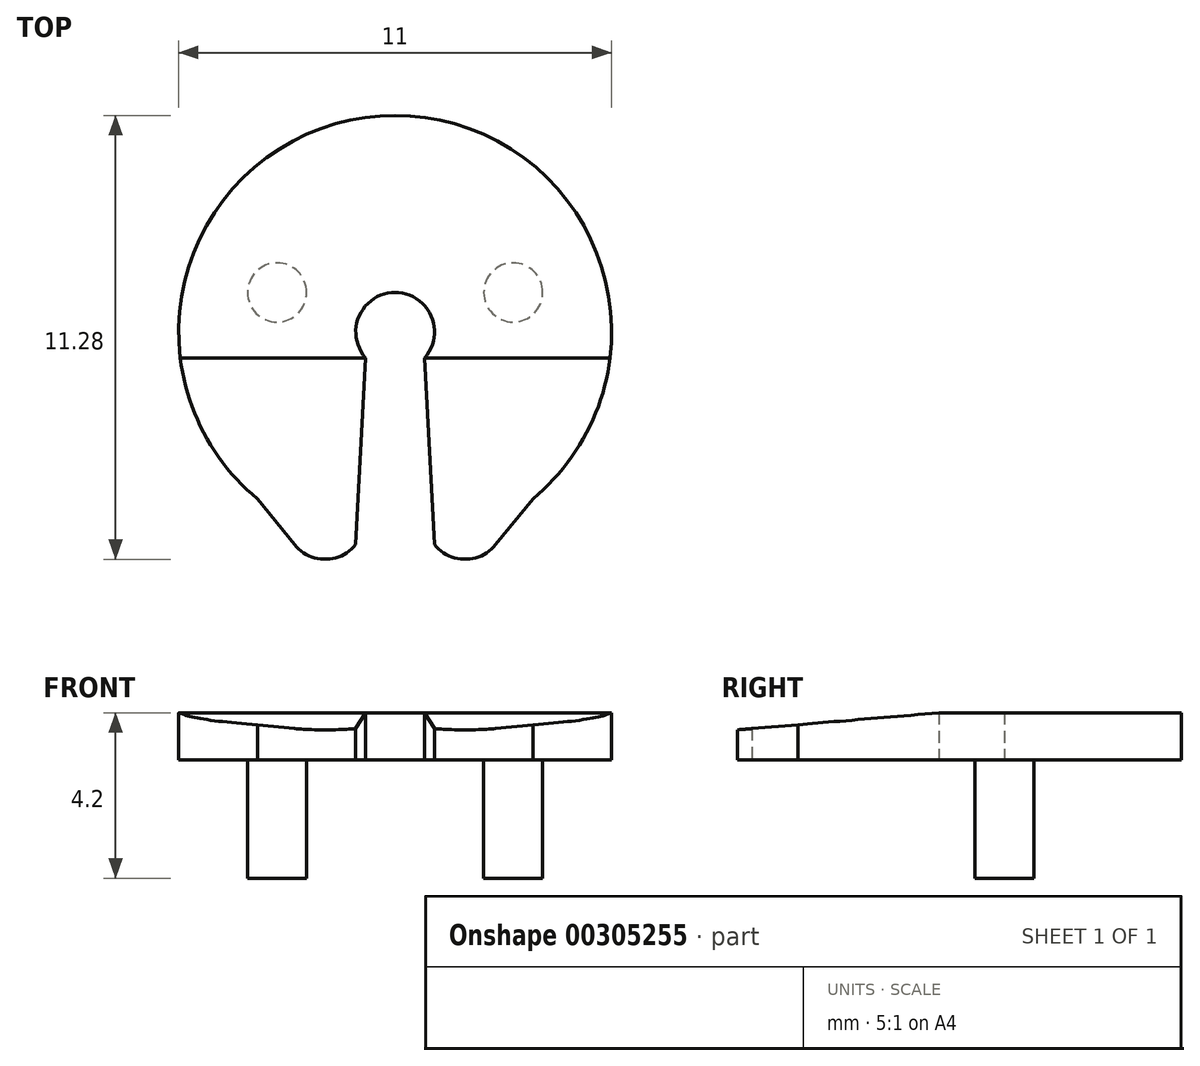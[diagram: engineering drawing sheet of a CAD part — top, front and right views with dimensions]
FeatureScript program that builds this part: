
annotation { "Feature Type Name" : "Feature", "Feature Type Description" : "" }
export const myFeature = defineFeature(function(context is Context, id is Id, definition is map)
    precondition{}
    {
        {
            var Q0;
            Q0=qCreatedBy(makeId("Top.planeOp"),FACE);
            var sketch = newSketch(context, id + "F0", { "sketchPlane" : qUnion([Q0])});
            skArc(sketch, "E0", {"start": v(0.75, -0.66) * mm, "mid": v(0, 1) * mm, "end": v(-0.75, -0.66) * mm});
            skArc(sketch, "E1", {"start": v(3.5, -4.24) * mm, "mid": v(0, 5.5) * mm, "end": v(-3.5, -4.24) * mm});
            skLineSegment(sketch, "E2", {"start": v(-3.5, -4.24) * mm, "end": v(3.5, -4.24) * mm, "construction": true});
            skLineSegment(sketch, "E3", {"start": v(-1, -5.4) * mm, "end": v(1, -5.4) * mm, "construction": true});
            skLineSegment(sketch, "E4", {"start": v(-0.75, -0.66) * mm, "end": v(-1, -5.4) * mm});
            skLineSegment(sketch, "E5", {"start": v(0.75, -0.66) * mm, "end": v(1, -5.4) * mm});
            skLineSegment(sketch, "E6", {"start": v(-0.75, -0.66) * mm, "end": v(0.75, -0.66) * mm, "construction": true});
            skLineSegment(sketch, "E7", {"start": v(3.5, -4.24) * mm, "end": v(2.56, -5.4) * mm});
            skLineSegment(sketch, "E8", {"start": v(-3.5, -4.24) * mm, "end": v(-2.56, -5.4) * mm});
            skArc(sketch, "E9", {"start": v(-2.56, -5.4) * mm, "mid": v(-1.78, -5.78) * mm, "end": v(-1, -5.4) * mm});
            skArc(sketch, "E10.MirrorCS", {"start": v(2.56, -5.4) * mm, "mid": v(1.78, -5.78) * mm, "end": v(1, -5.4) * mm});
            skLineSegment(sketch, "E11", {"start": v(0, 1) * mm, "end": v(3, 1) * mm, "construction": true});
            skCircle(sketch, "E12", {"center": v(3, 1) * mm, "radius": 0.75 * mm, "construction": true});
            skLineSegment(sketch, "E13.MirrorCS", {"start": v(0, 1) * mm, "end": v(-3, 1) * mm, "construction": true});
            skCircle(sketch, "E14.MirrorC", {"center": v(-3, 1) * mm, "radius": 0.75 * mm, "construction": true});
            skSolve(sketch);
        }
        {
            var Q0;
            Q0=makeQuery(id+"F0.imprint","IMPRINT",FACE,{"disambiguationData":[TD([[makeQuery(id+"F0.imprint","IMPRINT",EDGE,{"derivedFrom":sQuery(id+"F0.wireOp",EDGE,"E0")}),-1.0]])]});
            extrude(context, id + "F1", {"entities" : qUnion([Q0]), "depth" : 1.2 * mm});
        }
        {
            var Q0;
            Q0=qCreatedBy(makeId("Top.planeOp"),FACE);
            var sketch = newSketch(context, id + "F2", { "sketchPlane" : qUnion([Q0])});
            skCircle(sketch, "E15.0", {"center": v(-3, 1) * mm, "radius": 0.75 * mm});
            skCircle(sketch, "E16.0", {"center": v(3, 1) * mm, "radius": 0.75 * mm});
            skSolve(sketch);
        }
        {
            var Q0;
            Q0 = qSketchRegion(id + "F2", true);
            extrude(context, id + "F3", {"entities" : qUnion([Q0]), "operationType" : NewBodyOperationType.ADD, "oppositeDirection" : true, "depth" : 3 * mm});
        }
        {
            var Q0;
            Q0=makeQuery(id+"F1.opExtrude","SWEPT_FACE",FACE,{"disambiguationData":[OSD([sQuery(id+"F0.wireOp",EDGE,"E4")])]});
            var sketch = newSketch(context, id + "F4", { "sketchPlane" : qUnion([Q0])});
            skLineSegment(sketch, "E17", {"start": v(-5.45, 0) * mm, "end": v(-5.45, 0.8) * mm, "construction": true});
            skSolve(sketch);
        }
        {
            var Q0;
            Q0=makeQuery(id+"F1.opExtrude","CAP_VERTEX",VERTEX,{"disambiguationData":[OSD([sQuery(id+"F0.wireOp",EDGE,"E0"),sQuery(id+"F0.wireOp",EDGE,"E4")])],"isStart":false});
            var Q1;
            Q1=makeQuery(id+"F1.opExtrude","CAP_VERTEX",VERTEX,{"disambiguationData":[OSD([sQuery(id+"F0.wireOp",EDGE,"E0"),sQuery(id+"F0.wireOp",EDGE,"E5")])],"isStart":false});
            var Q2;
            Q2=sQuery(id+"F4.wireOp",VERTEX,"E17.end");
            cPlane(context, id + "F5", {"entities" : qUnion([Q0, Q1, Q2]), "cplaneType" : CPlaneType.THREE_POINT, "offset" : 25 * mm, "width" : 150 * mm, "height" : 150 * mm});
        }
        {
            var Q0;
            Q0=qCreatedBy(id+"F5.planeOp",FACE);
            var sketch = newSketch(context, id + "F6", { "sketchPlane" : qUnion([Q0])});
            skLineSegment(sketch, "E18", {"start": v(-0.75, -0.56) * mm, "end": v(-5.46, -0.56) * mm});
            skLineSegment(sketch, "E19", {"start": v(5.46, -0.56) * mm, "end": v(0.75, -0.56) * mm});
            skLineSegment(sketch, "E20.bottom", {"start": v(-5.46, -0.56) * mm, "end": v(5.46, -0.56) * mm});
            skLineSegment(sketch, "E20.top", {"start": v(-5.46, -5.93) * mm, "end": v(5.46, -5.93) * mm});
            skLineSegment(sketch, "E20.left", {"start": v(-5.46, -0.56) * mm, "end": v(-5.46, -5.93) * mm});
            skLineSegment(sketch, "E20.right", {"start": v(5.46, -0.56) * mm, "end": v(5.46, -5.93) * mm});
            skPoint(sketch, "E21.0.start.orphan", {"position": v(-3.5, -4.13) * mm});
            skPoint(sketch, "E22.0.start.orphan", {"position": v(-2.56, -5.29) * mm});
            skPoint(sketch, "E23.0.end.orphan", {"position": v(-1, -5.29) * mm});
            skPoint(sketch, "E23.0.start.orphan", {"position": v(-0.75, -0.56) * mm});
            skPoint(sketch, "E24.0.start.orphan", {"position": v(0.75, -0.56) * mm});
            skPoint(sketch, "E25.0.start.orphan", {"position": v(1, -5.29) * mm});
            skPoint(sketch, "E26.0.end.orphan", {"position": v(2.56, -5.29) * mm});
            skPoint(sketch, "E27.0.start.orphan", {"position": v(3.5, -4.13) * mm});
            skSolve(sketch);
        }
        {
            var Q0;
            Q0 = qSketchRegion(id + "F6", true);
            var Q1;
            Q1=makeQuery(id+"F1.opExtrude","CAP_FACE",FACE,{"disambiguationData":[OSD([sQuery(id+"F0.wireOp",EDGE,"E0"),sQuery(id+"F0.wireOp",EDGE,"E1"),sQuery(id+"F0.wireOp",EDGE,"E4"),sQuery(id+"F0.wireOp",EDGE,"E5"),sQuery(id+"F0.wireOp",EDGE,"E7"),sQuery(id+"F0.wireOp",EDGE,"E8"),sQuery(id+"F0.wireOp",EDGE,"E9"),sQuery(id+"F0.wireOp",EDGE,"E10.MirrorCS")])],"isStart":false});
            extrude(context, id + "F7", {"entities" : qUnion([Q0]), "operationType" : NewBodyOperationType.REMOVE, "endBound" : BoundingType.UP_TO_SURFACE, "endBoundEntityFace" : qUnion([Q1]), "depth" : 25 * mm});
        }
    });
